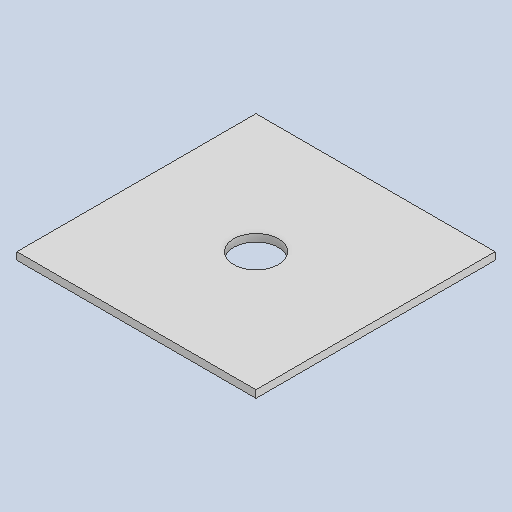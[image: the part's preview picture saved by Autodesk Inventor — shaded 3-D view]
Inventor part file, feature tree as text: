
AUTODESK INVENTOR PART (.ipt)
format: ipt  version: 2023 (Build 270158030, 158C)  size: 87,552 bytes
history: native  units: in
note: dims shown in document units (in); Inventor stores cm internally (conversion verified against a paired STEP export)
features: extrude x1, sketch x1
ambient origin geometry x8: Origin, YZ Plane, XZ Plane, XY Plane, X Axis, Y Axis, Z Axis, Center Point
bodies: Solid1 (feature_tree)
feature tree (2):
  extrude  "Extrusion1"  Depth=8.0in
  sketch  "Sketch1"  dims[d0=8.0in d1=8.0in d2=0.25in d3=0.0in d4=1.5in d5=4.0in d6=4.0in]
